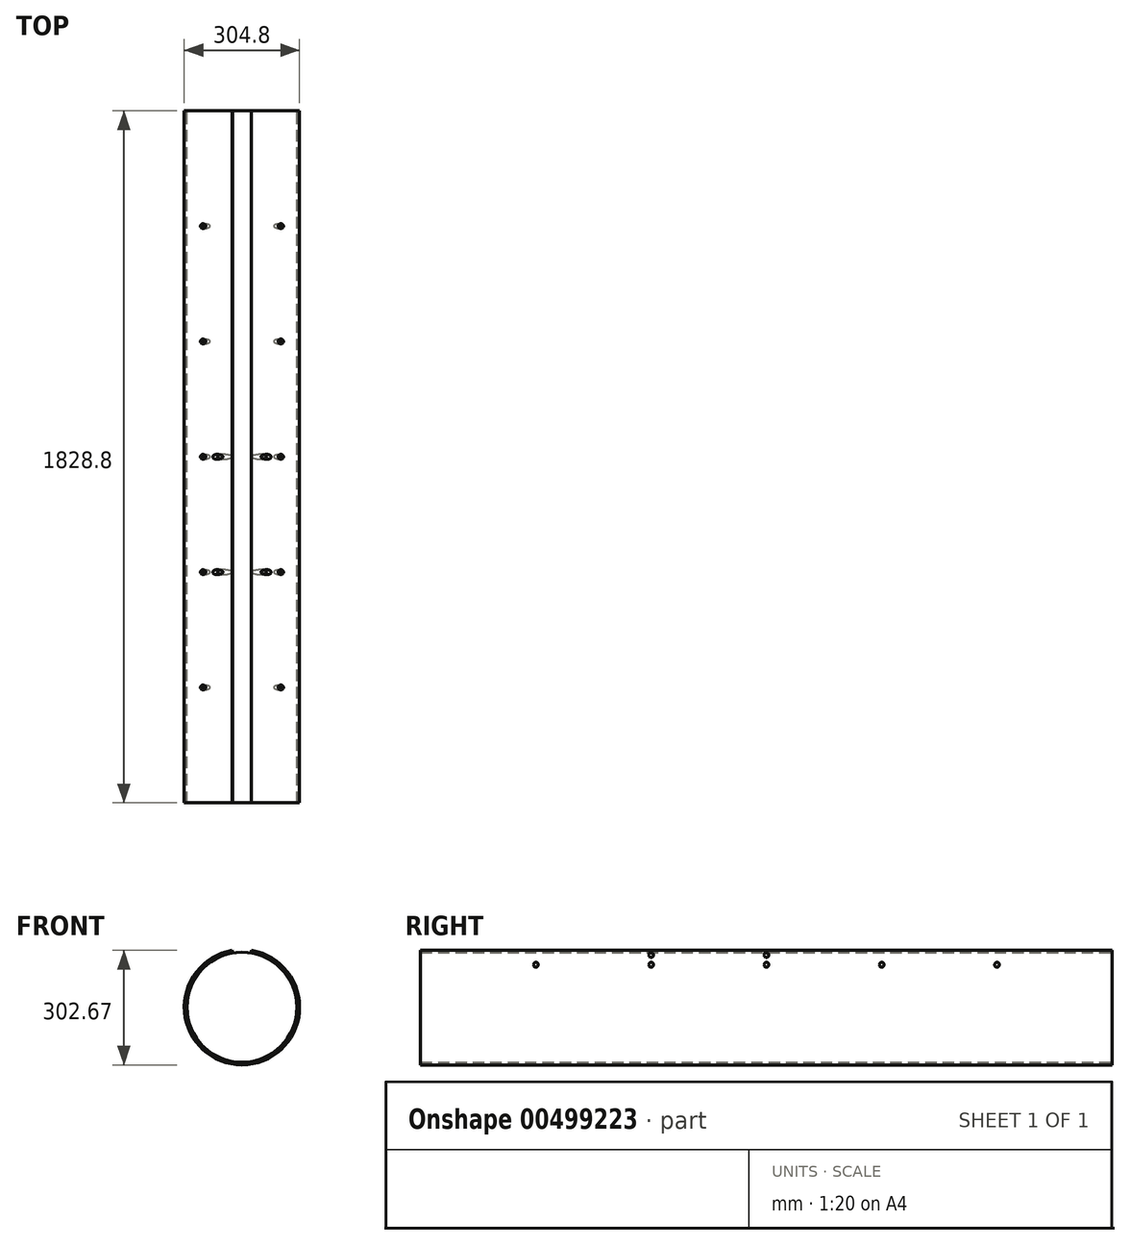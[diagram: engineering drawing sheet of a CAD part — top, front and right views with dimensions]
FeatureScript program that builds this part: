
annotation { "Feature Type Name" : "Feature", "Feature Type Description" : "" }
export const myFeature = defineFeature(function(context is Context, id is Id, definition is map)
    precondition{}
    {
        {
            var Q0;
            Q0=qCreatedBy(makeId("Front.planeOp"),FACE);
            var sketch = newSketch(context, id + "F0", { "sketchPlane" : qUnion([Q0])});
            skArc(sketch, "E0", {"start": v(-25.4, 150.27) * mm, "mid": v(0, -152.4) * mm, "end": v(25.4, 150.27) * mm});
            skArc(sketch, "E1", {"start": v(-24.34, 144) * mm, "mid": v(0, -146.05) * mm, "end": v(24.34, 144) * mm});
            skLineSegment(sketch, "E2", {"start": v(-24.34, 144) * mm, "end": v(-25.4, 150.27) * mm});
            skLineSegment(sketch, "E3", {"start": v(24.34, 144) * mm, "end": v(25.4, 150.27) * mm});
            skPoint(sketch, "E4.end.orphan", {"position": v(0, 152.4) * mm});
            skSolve(sketch);
        }
        {
            var Q0;
            Q0 = qSketchRegion(id + "F0", true);
            extrude(context, id + "F1", {"entities" : qUnion([Q0]), "endBound" : BoundingType.SYMMETRIC, "depth" : 1828.8 * mm});
        }
        {
            var Q0;
            Q0=qCreatedBy(makeId("Right.planeOp"),FACE);
            var sketch = newSketch(context, id + "F2", { "sketchPlane" : qUnion([Q0])});
            skLineSegment(sketch, "E5.0", {"start": v(-914.4, 150.27) * mm, "end": v(914.4, 150.27) * mm});
            skCircle(sketch, "E6", {"center": v(0, 112.17) * mm, "radius": 6.35 * mm});
            skCircle(sketch, "E7", {"center": v(304.8, 112.17) * mm, "radius": 6.35 * mm});
            skCircle(sketch, "E8", {"center": v(609.6, 112.17) * mm, "radius": 6.35 * mm});
            skCircle(sketch, "E9", {"center": v(-304.8, 112.17) * mm, "radius": 6.35 * mm});
            skCircle(sketch, "E10", {"center": v(-609.6, 112.17) * mm, "radius": 6.35 * mm});
            skSolve(sketch);
        }
        {
            var Q0;
            Q0 = qSketchRegion(id + "F2", true);
            extrude(context, id + "F3", {"entities" : qUnion([Q0]), "operationType" : NewBodyOperationType.REMOVE, "oppositeDirection" : true, "depth" : 203.2 * mm, "hasSecondDirection" : true, "secondDirectionOppositeDirection" : false, "secondDirectionDepth" : 203.2 * mm});
        }
        {
            var Q0;
            Q0=qCreatedBy(makeId("Right.planeOp"),FACE);
            var sketch = newSketch(context, id + "F4", { "sketchPlane" : qUnion([Q0])});
            skCircle(sketch, "E11", {"center": v(0, 137.57) * mm, "radius": 6.35 * mm});
            skCircle(sketch, "E12", {"center": v(-304.8, 137.57) * mm, "radius": 6.35 * mm});
            skSolve(sketch);
        }
        {
            var Q0;
            Q0 = qSketchRegion(id + "F4", true);
            extrude(context, id + "F5", {"entities" : qUnion([Q0]), "operationType" : NewBodyOperationType.REMOVE, "depth" : 203.2 * mm, "hasSecondDirection" : true, "secondDirectionOppositeDirection" : true, "secondDirectionDepth" : 203.2 * mm});
        }
        {
            var Q0;
            Q0=qCreatedBy(makeId("Front.planeOp"),FACE);
            var sketch = newSketch(context, id + "F6", { "sketchPlane" : qUnion([Q0])});
            skCircle(sketch, "E13", {"center": v(0, 0) * mm, "radius": 145.42 * mm});
            skSolve(sketch);
        }
        {
            var Q0;
            Q0 = qSketchRegion(id + "F6", true);
            extrude(context, id + "F7", {"entities" : qUnion([Q0]), "endBound" : BoundingType.SYMMETRIC, "depth" : 1828.8 * mm});
        }
    });
